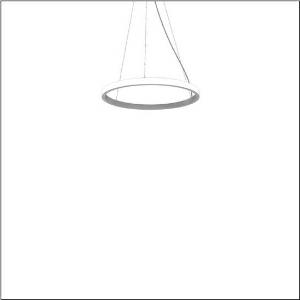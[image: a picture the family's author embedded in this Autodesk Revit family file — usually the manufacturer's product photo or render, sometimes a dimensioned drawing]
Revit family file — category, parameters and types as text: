
# Revit family: silica_r__21_ring-o_5pjbo1d3204a_6aba
name_source: partatom
category: Lighting Fixtures
units: mm (PartAtom-declared; Revit-internal decimal feet)

## family parameters
Cut with Voids When Loaded = No
Host = Face
Light Source = No
Part Type = Normal
Room Calculation Point = No
Round Connector Dimension = Use Diameter
Shared = No

## types (1)
- Silica® 21 Ring-O (1 x LED, 3930 lm, 60 W, 4000K)
    Apparent Load = 60 VA
    CIE Flux Codes = 2 16 49 50 100
    Color Rendering = 80
    Color Temperature = 4000K
    Default Elevation = 1800 mm
    Description = Silica® 21 Ring-O, suspended luminaire, of PMMA, frosted, light emission: outer ring side luminous distribution, primary light characteristic: symmetric, installation type: suspended mounting, LED, rated luminous flux: 3.930lm, luminous efficacy: 66lm/W, light colour: 840, colour temperature: 4000K, control gear: DALI 2, with terminal, 5-pole, mains connection: 230V, AC/DC, 0/50..60Hz, rated input power: 60W, housing, of extruded aluminium section, metallic grey (RAL 9006), diameter: 610mm, ceiling canopy, metallic grey (RAL 9006), protection rating (lamp compartment): IP40, insulation class (complete): insulation class I (protective earthing), certification: CE, impact resistance: IK02, permissible operating ambient temperature: 0..+35°C, packaging unit: 1 piece
    Height = 48 mm  [stored 0.15748 ft]
    Lamp = 1 x LED
    Lamp Light Flux = 3930 lm
    Lamp Power = 60 W
    Lamp count = 1
    Length = 610 mm
    Luminous efficacy = 66 lm/W
    Manufacturer = Siteco
    ModVariant = No
    Model = 5PJBO1D3204A
    Mounting Place = Ceiling
    Mounting Type = Pendant
    Number of Poles = 1
    OnlyDefault = Yes
    Power Factor = 1
    Product Name = Silica® 21 Ring-O
    Product group = suspended luminaire
    ProductGroupID = 905
    Protection Class = Protection class I
    Protection Degree = IP 40
    RLX_Detail_Level = 1
    RLX_Emergency_Light_Flux = 0 lm
    RLX_Emergency_Type = 0
    RLX_Emergency_Type_DB = No
    RlxData = <blob elided: 11645 chars, md5=aa74ad91>
    Socket = socket
    Standby Power = 0 W
    System Light Flux = 3930 lm
    System Power = 60 W
    Type Comments = Product without accessories
    Type Image = l_1251758.jpg
    URL = http://relux.com
    VarID = ---
    Voltage = 0 V
    Weight = 0.00 kg
    Width = 0 mm  [stored 0 ft]

note: [stored X ft] marks values corroborated as IEEE doubles in the binary element streams (Revit-internal decimal feet)

## geometry (parser evidence)
native form markers: Sweep x10
no freeform markers — native parametric forms only
